# Revit family: NaughtOne_Symbol45DegreeCurveLounge
name_source: partatom
category: Furniture
units: mm (PartAtom-declared; Revit-internal decimal feet)

## family parameters
Always vertical = Yes
Cut with Voids When Loaded = No
Enable Cutting in Views = No
OmniClass Number = 23.40.20.00
OmniClass Title = General Furniture and Specialties
Render Appearance Source = Family Geometry
Room Calculation Point = No
Shared = Yes
Work Plane-Based = No

## types (1)
- 45 degree curve bench single fabric Lounge Ht
    45 degree curve bench = Yes
    45 degree curve seat = No
    Assembly Code = E2020200
    Default Elevation = 0 "
    Description = Symbol 45 Degree Curve 45 degree curve bench lounge height 16 inch seat height single fabric
    External 45 degree curve = No
    Manufacturer = Herman Miller, Inc.
    Model = NOSYN510L1
    Package Qty = 1
    Type = 1
    URL = http://www.hermanmiller.com

## geometry (parser evidence)
native form markers: Sweep x6
no freeform markers — native parametric forms only
